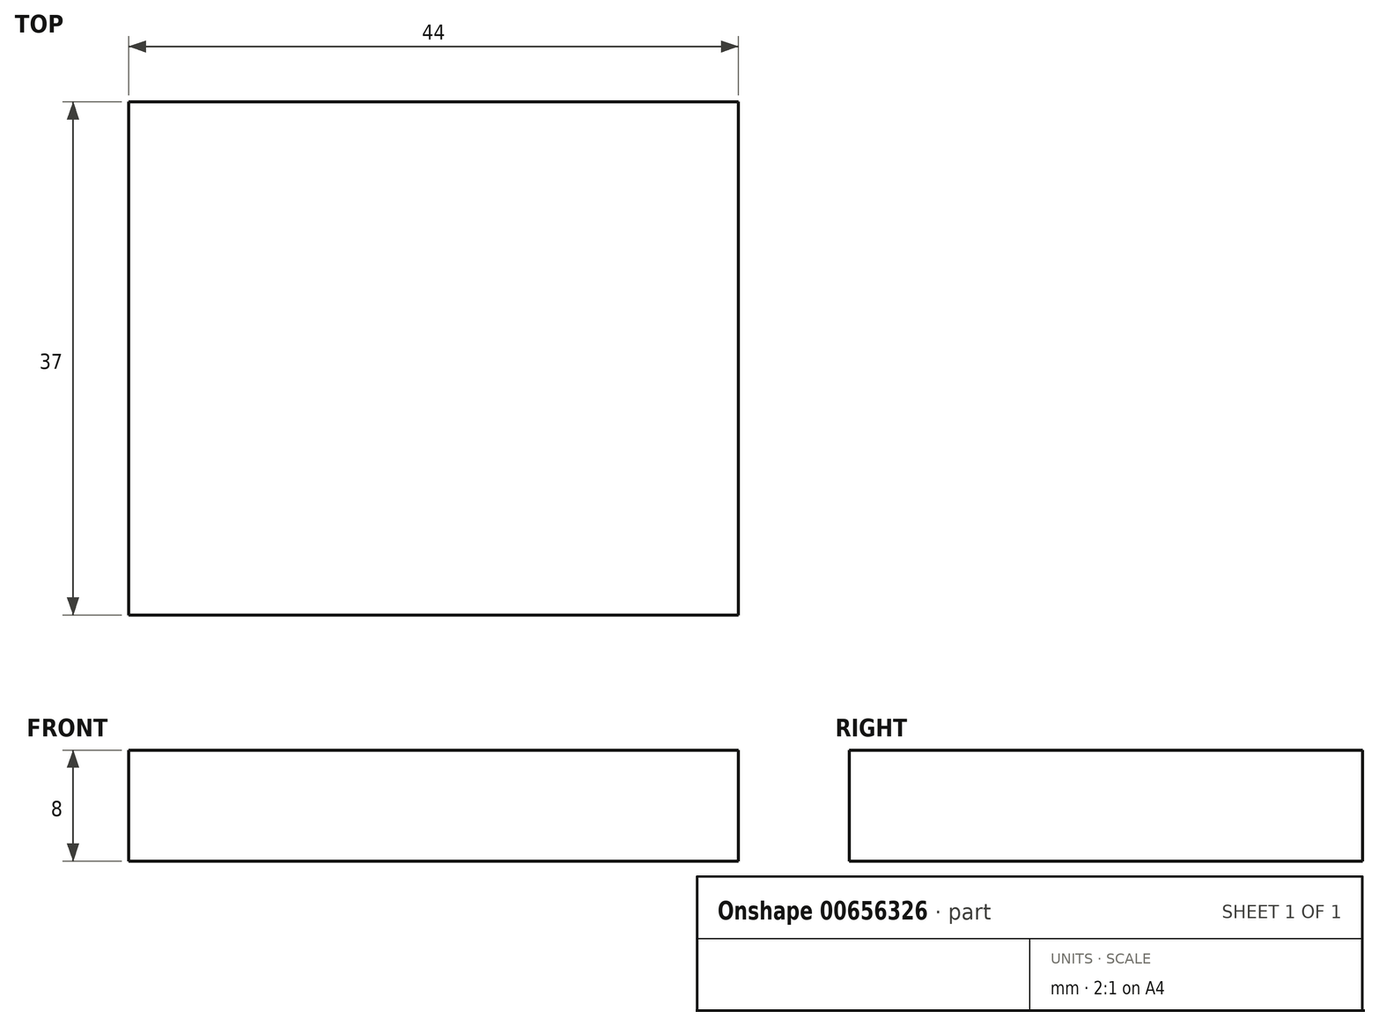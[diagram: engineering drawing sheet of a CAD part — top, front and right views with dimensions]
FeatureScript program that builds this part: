
annotation { "Feature Type Name" : "Feature", "Feature Type Description" : "" }
export const myFeature = defineFeature(function(context is Context, id is Id, definition is map)
    precondition{}
    {
        {
            var Q0;
            Q0=qCreatedBy(makeId("Top.planeOp"),FACE);
            var sketch = newSketch(context, id + "F0", { "sketchPlane" : qUnion([Q0])});
            skLineSegment(sketch, "E0.bottom", {"start": v(22, 18.5) * mm, "end": v(-22, 18.5) * mm});
            skLineSegment(sketch, "E0.top", {"start": v(22, -18.5) * mm, "end": v(-22, -18.5) * mm});
            skLineSegment(sketch, "E0.left", {"start": v(22, 18.5) * mm, "end": v(22, -18.5) * mm});
            skLineSegment(sketch, "E0.right", {"start": v(-22, 18.5) * mm, "end": v(-22, -18.5) * mm});
            skPoint(sketch, "E0.middle", {"position": v(0, 0) * mm});
            skSolve(sketch);
        }
        {
            var Q0;
            Q0 = qSketchRegion(id + "F0", true);
            extrude(context, id + "F1", {"entities" : qUnion([Q0]), "depth" : 8 * mm, "offsetDistance" : 25 * mm});
        }
    });
